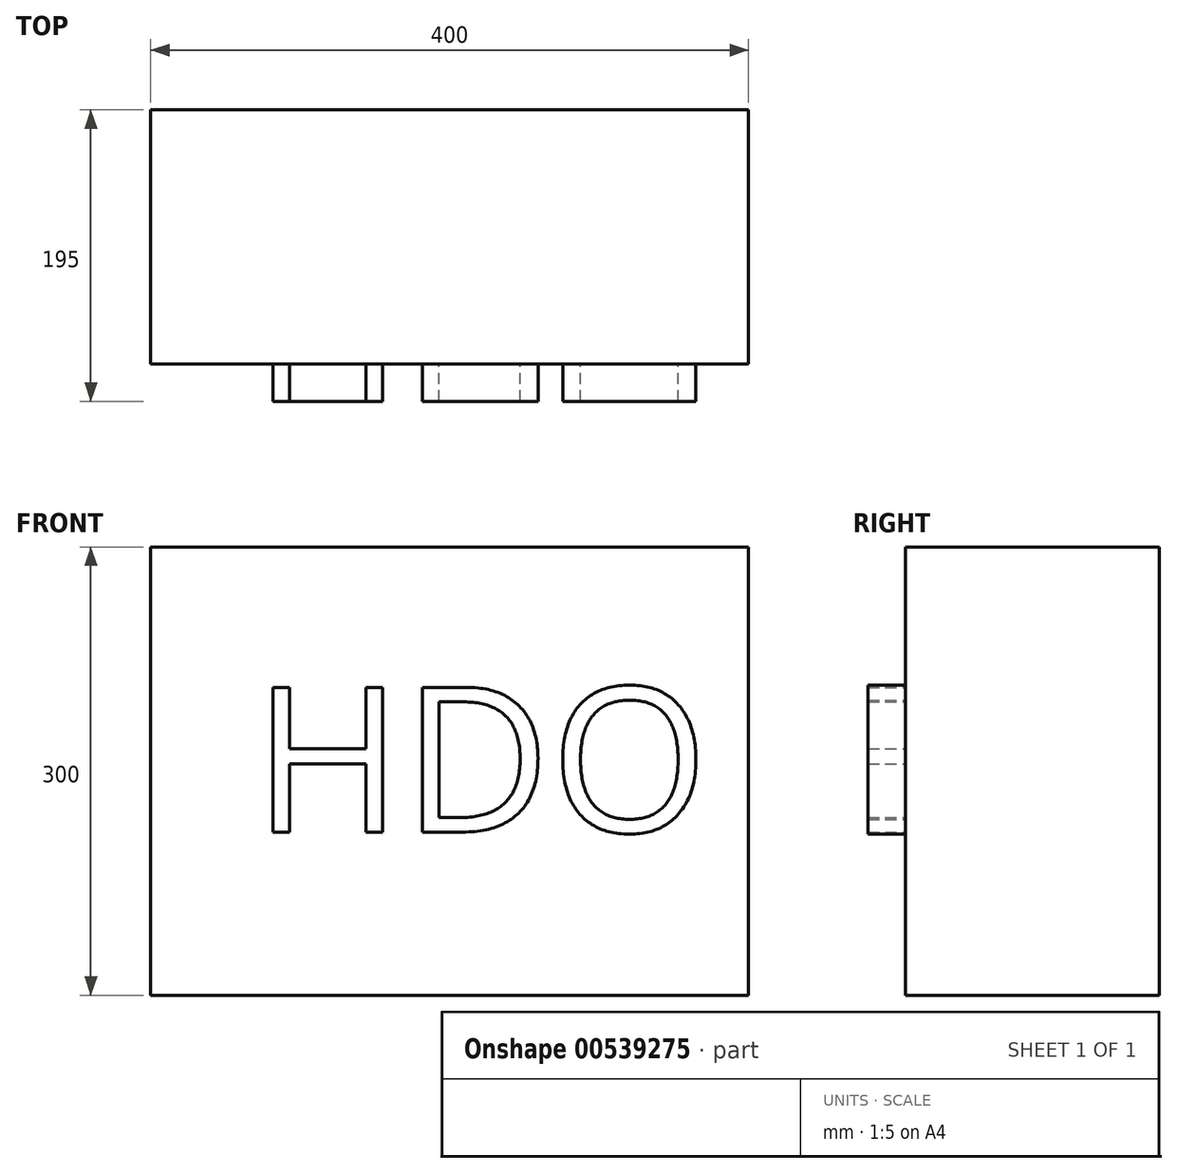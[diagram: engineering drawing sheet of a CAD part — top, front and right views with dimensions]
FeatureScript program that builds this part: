
annotation { "Feature Type Name" : "Feature", "Feature Type Description" : "" }
export const myFeature = defineFeature(function(context is Context, id is Id, definition is map)
    precondition{}
    {
        {
            var Q0;
            Q0=qCreatedBy(makeId("Front.planeOp"),FACE);
            var sketch = newSketch(context, id + "F0", { "sketchPlane" : qUnion([Q0])});
            skLineSegment(sketch, "E0.bottom", {"start": v(-200, -150) * mm, "end": v(200, -150) * mm});
            skLineSegment(sketch, "E0.top", {"start": v(-200, 150) * mm, "end": v(200, 150) * mm});
            skLineSegment(sketch, "E0.left", {"start": v(-200, -150) * mm, "end": v(-200, 150) * mm});
            skLineSegment(sketch, "E0.right", {"start": v(200, -150) * mm, "end": v(200, 150) * mm});
            skPoint(sketch, "E0.middle", {"position": v(0, 0) * mm});
            skSolve(sketch);
        }
        {
            var Q0;
            Q0=makeQuery(id+"F0.imprint","IMPRINT",FACE,{"disambiguationData":[TD([[makeQuery(id+"F0.imprint","IMPRINT",EDGE,{"derivedFrom":sQuery(id+"F0.wireOp",EDGE,"E0.bottom")}),1.0]])]});
            extrude(context, id + "F1", {"entities" : qUnion([Q0]), "endBound" : BoundingType.SYMMETRIC, "depth" : 170 * mm, "offsetDistance" : 25 * mm});
        }
        {
            var Q0;
            Q0=makeQuery(id+"F1.opExtrude","CAP_FACE",FACE,{"disambiguationData":[OSD([sQuery(id+"F0.wireOp",EDGE,"E0.bottom"),sQuery(id+"F0.wireOp",EDGE,"E0.top"),sQuery(id+"F0.wireOp",EDGE,"E0.left"),sQuery(id+"F0.wireOp",EDGE,"E0.right")])],"isStart":false});
            var sketch = newSketch(context, id + "F2", { "sketchPlane" : qUnion([Q0])});
            skText(sketch, "E1", { "text": "HDO\n", "fontName": "OpenSans-Regular.ttf"});
            const initialGuessF2  = {"E1": [-0.13163, -0.04083, 1, 0, 0.09769]};
            skSetInitialGuess(sketch, initialGuessF2);
            skSolve(sketch);
        }
        {
            var Q0;
            Q0 = qSketchRegion(id + "F2", true);
            extrude(context, id + "F3", {"entities" : qUnion([Q0]), "operationType" : NewBodyOperationType.ADD, "depth" : 25 * mm, "offsetDistance" : 25 * mm});
        }
    });
